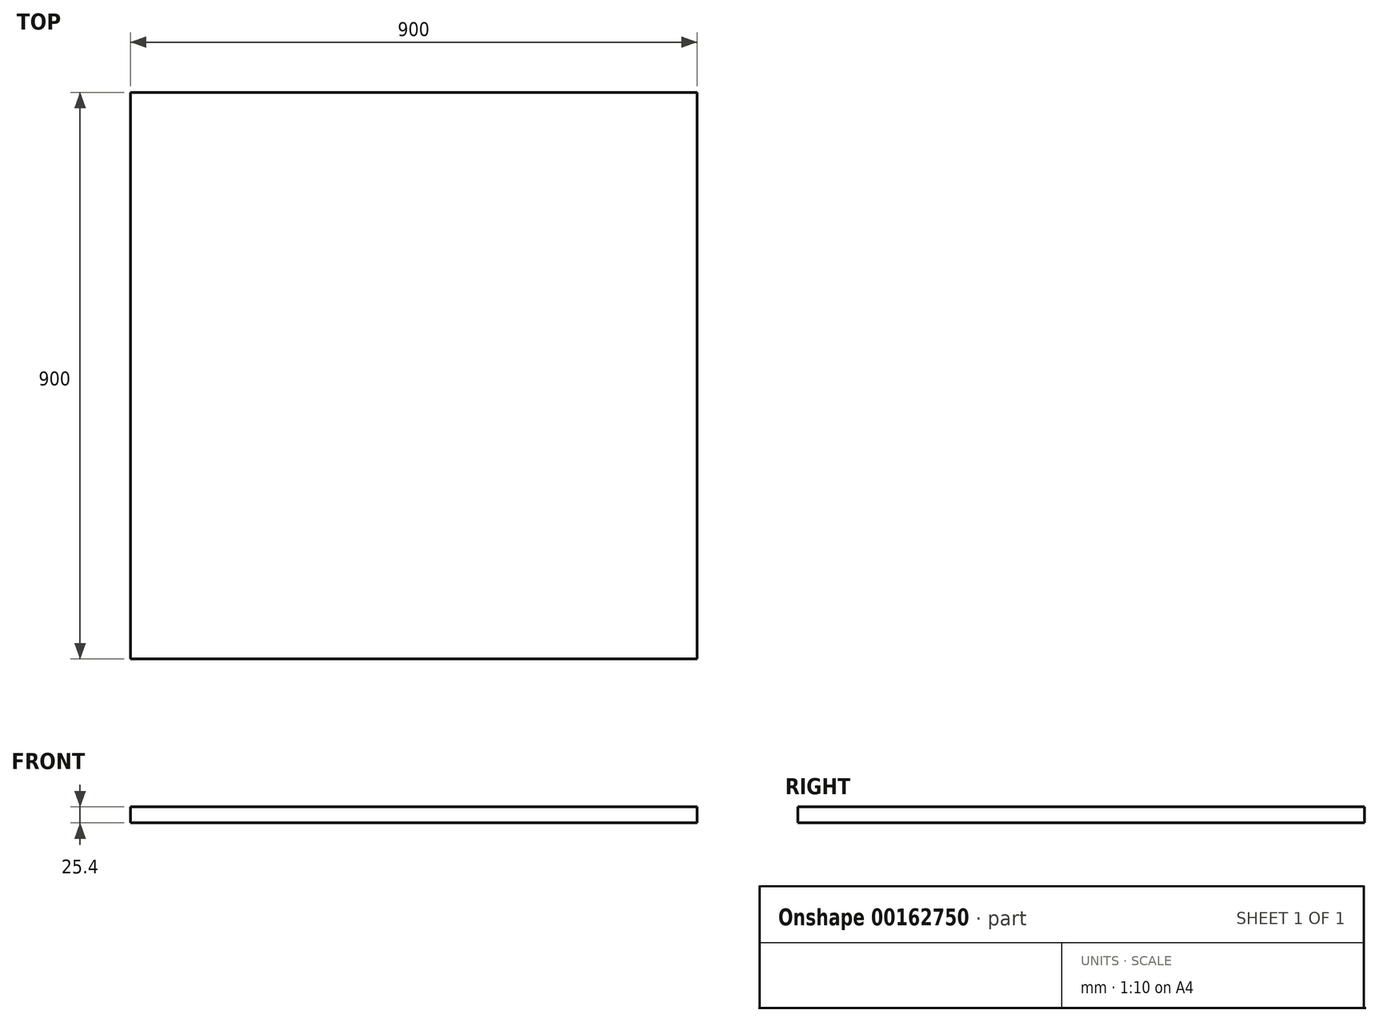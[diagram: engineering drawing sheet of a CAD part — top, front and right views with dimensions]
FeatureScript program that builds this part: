
annotation { "Feature Type Name" : "Feature", "Feature Type Description" : "" }
export const myFeature = defineFeature(function(context is Context, id is Id, definition is map)
    precondition{}
    {
        {
            var Q0;
            Q0=qCreatedBy(makeId("Top.planeOp"),FACE);
            var sketch = newSketch(context, id + "F0", { "sketchPlane" : qUnion([Q0])});
            skLineSegment(sketch, "E0.bottom", {"start": v(-450, -450) * mm, "end": v(450, -450) * mm});
            skLineSegment(sketch, "E0.top", {"start": v(-450, 450) * mm, "end": v(450, 450) * mm});
            skLineSegment(sketch, "E0.left", {"start": v(-450, -450) * mm, "end": v(-450, 450) * mm});
            skLineSegment(sketch, "E0.right", {"start": v(450, -450) * mm, "end": v(450, 450) * mm});
            skLineSegment(sketch, "E1", {"start": v(-450, -450) * mm, "end": v(0, 0) * mm, "construction": true});
            skLineSegment(sketch, "E2", {"start": v(-450, 450) * mm, "end": v(450, -450) * mm, "construction": true});
            skSolve(sketch);
        }
        {
            var Q0;
            Q0=makeQuery(id+"F0.imprint","IMPRINT",FACE,{"disambiguationData":[TD([[makeQuery(id+"F0.imprint","IMPRINT",EDGE,{"derivedFrom":sQuery(id+"F0.wireOp",EDGE,"E0.bottom")}),1.0]])]});
            extrude(context, id + "F1", {"entities" : qUnion([Q0]), "depth" : 25.4 * mm});
        }
    });
